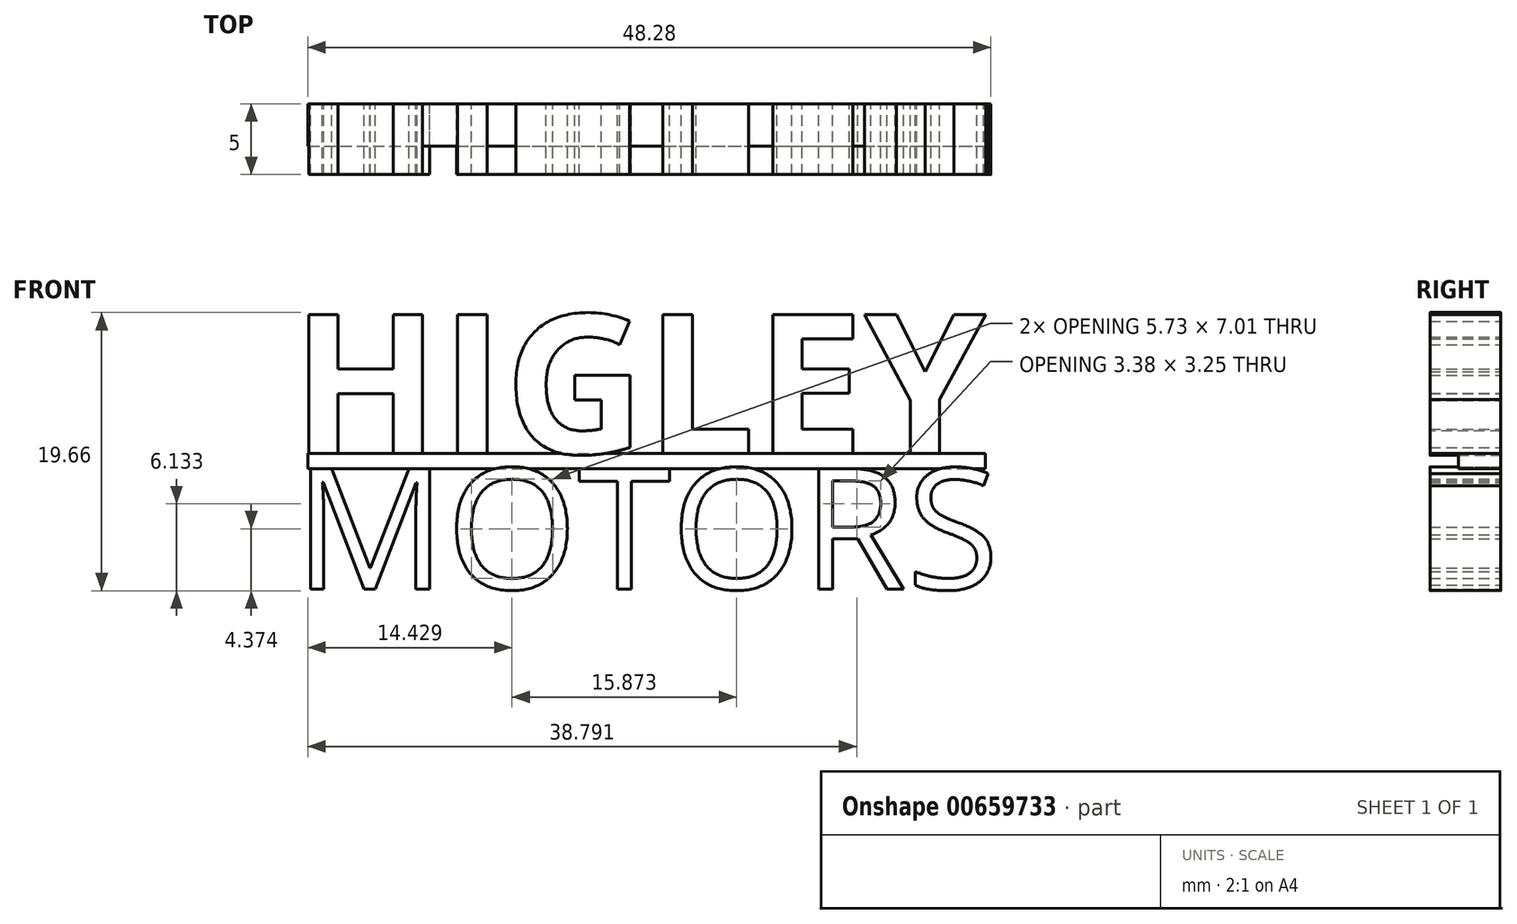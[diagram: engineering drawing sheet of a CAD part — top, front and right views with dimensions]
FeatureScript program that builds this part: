
annotation { "Feature Type Name" : "Feature", "Feature Type Description" : "" }
export const myFeature = defineFeature(function(context is Context, id is Id, definition is map)
    precondition{}
    {
        {
            var Q0;
            Q0=qCreatedBy(makeId("Front.planeOp"),FACE);
            var sketch = newSketch(context, id + "F0", { "sketchPlane" : qUnion([Q0])});
            skText(sketch, "E0", { "text": "HIGLEY", "fontName": "OpenSans-Bold.ttf"});
            const initialGuessF0  = {"E0": [-0.0133, 0, 1, 0, 0.0099]};
            skSetInitialGuess(sketch, initialGuessF0);
            skSolve(sketch);
        }
        {
            var Q0;
            Q0 = qSketchRegion(id + "F0", true);
            extrude(context, id + "F1", {"entities" : qUnion([Q0]), "depth" : 5 * mm, "offsetDistance" : 25 * mm});
        }
        {
            var Q0;
            Q0=qCreatedBy(makeId("Front.planeOp"),FACE);
            var sketch = newSketch(context, id + "F2", { "sketchPlane" : qUnion([Q0])});
            skText(sketch, "E1", { "text": "MOTORS", "fontName": "OpenSans-Regular.ttf"});
            const initialGuessF2  = {"E1": [-0.0116, -0.00858, 1, 0, 0.00858]};
            skSetInitialGuess(sketch, initialGuessF2);
            skSolve(sketch);
        }
        {
            var Q0;
            Q0 = qSketchRegion(id + "F2", true);
            extrude(context, id + "F3", {"entities" : qUnion([Q0]), "depth" : 5 * mm, "offsetDistance" : 25 * mm});
        }
        {
            var Q0;
            Q0=makeQuery(id+"F3.opExtrude","SWEPT_BODY",BODY,{"disambiguationData":[OSD([sQuery(id+"F2.wireOp",EDGE,"E1.sketch_text.stroke-0"),sQuery(id+"F2.wireOp",EDGE,"E1.sketch_text.stroke-1"),sQuery(id+"F2.wireOp",EDGE,"E1.sketch_text.stroke-2"),sQuery(id+"F2.wireOp",EDGE,"E1.sketch_text.stroke-3"),sQuery(id+"F2.wireOp",EDGE,"E1.sketch_text.stroke-4"),sQuery(id+"F2.wireOp",EDGE,"E1.sketch_text.stroke-5"),sQuery(id+"F2.wireOp",EDGE,"E1.sketch_text.stroke-6"),sQuery(id+"F2.wireOp",EDGE,"E1.sketch_text.stroke-7"),sQuery(id+"F2.wireOp",EDGE,"E1.sketch_text.stroke-8"),sQuery(id+"F2.wireOp",EDGE,"E1.sketch_text.stroke-9"),sQuery(id+"F2.wireOp",EDGE,"E1.sketch_text.stroke-10"),sQuery(id+"F2.wireOp",EDGE,"E1.sketch_text.stroke-11"),sQuery(id+"F2.wireOp",EDGE,"E1.sketch_text.stroke-12"),sQuery(id+"F2.wireOp",EDGE,"E1.sketch_text.stroke-13"),sQuery(id+"F2.wireOp",EDGE,"E1.sketch_text.stroke-14"),sQuery(id+"F2.wireOp",EDGE,"E1.sketch_text.stroke-15"),sQuery(id+"F2.wireOp",EDGE,"E1.sketch_text.stroke-16"),sQuery(id+"F2.wireOp",EDGE,"E1.sketch_text.stroke-17")])]});
            var Q1;
            Q1=makeQuery(id+"F3.opExtrude","SWEPT_BODY",BODY,{"disambiguationData":[OSD([sQuery(id+"F2.wireOp",EDGE,"E1.sketch_text.stroke-18"),sQuery(id+"F2.wireOp",EDGE,"E1.sketch_text.stroke-19"),sQuery(id+"F2.wireOp",EDGE,"E1.sketch_text.stroke-20"),sQuery(id+"F2.wireOp",EDGE,"E1.sketch_text.stroke-21"),sQuery(id+"F2.wireOp",EDGE,"E1.sketch_text.stroke-22"),sQuery(id+"F2.wireOp",EDGE,"E1.sketch_text.stroke-23"),sQuery(id+"F2.wireOp",EDGE,"E1.sketch_text.stroke-24"),sQuery(id+"F2.wireOp",EDGE,"E1.sketch_text.stroke-25"),sQuery(id+"F2.wireOp",EDGE,"E1.sketch_text.stroke-26"),sQuery(id+"F2.wireOp",EDGE,"E1.sketch_text.stroke-27"),sQuery(id+"F2.wireOp",EDGE,"E1.sketch_text.stroke-28"),sQuery(id+"F2.wireOp",EDGE,"E1.sketch_text.stroke-29"),sQuery(id+"F2.wireOp",EDGE,"E1.sketch_text.stroke-30"),sQuery(id+"F2.wireOp",EDGE,"E1.sketch_text.stroke-31"),sQuery(id+"F2.wireOp",EDGE,"E1.sketch_text.stroke-32"),sQuery(id+"F2.wireOp",EDGE,"E1.sketch_text.stroke-33")])]});
            var Q2;
            Q2=makeQuery(id+"F3.opExtrude","SWEPT_BODY",BODY,{"disambiguationData":[OSD([sQuery(id+"F2.wireOp",EDGE,"E1.sketch_text.stroke-34"),sQuery(id+"F2.wireOp",EDGE,"E1.sketch_text.stroke-35"),sQuery(id+"F2.wireOp",EDGE,"E1.sketch_text.stroke-36"),sQuery(id+"F2.wireOp",EDGE,"E1.sketch_text.stroke-37"),sQuery(id+"F2.wireOp",EDGE,"E1.sketch_text.stroke-38"),sQuery(id+"F2.wireOp",EDGE,"E1.sketch_text.stroke-39"),sQuery(id+"F2.wireOp",EDGE,"E1.sketch_text.stroke-40"),sQuery(id+"F2.wireOp",EDGE,"E1.sketch_text.stroke-41")])]});
            var Q3;
            Q3=makeQuery(id+"F3.opExtrude","SWEPT_BODY",BODY,{"disambiguationData":[OSD([sQuery(id+"F2.wireOp",EDGE,"E1.sketch_text.stroke-42"),sQuery(id+"F2.wireOp",EDGE,"E1.sketch_text.stroke-43"),sQuery(id+"F2.wireOp",EDGE,"E1.sketch_text.stroke-44"),sQuery(id+"F2.wireOp",EDGE,"E1.sketch_text.stroke-45"),sQuery(id+"F2.wireOp",EDGE,"E1.sketch_text.stroke-46"),sQuery(id+"F2.wireOp",EDGE,"E1.sketch_text.stroke-47"),sQuery(id+"F2.wireOp",EDGE,"E1.sketch_text.stroke-48"),sQuery(id+"F2.wireOp",EDGE,"E1.sketch_text.stroke-49"),sQuery(id+"F2.wireOp",EDGE,"E1.sketch_text.stroke-50"),sQuery(id+"F2.wireOp",EDGE,"E1.sketch_text.stroke-51"),sQuery(id+"F2.wireOp",EDGE,"E1.sketch_text.stroke-52"),sQuery(id+"F2.wireOp",EDGE,"E1.sketch_text.stroke-53"),sQuery(id+"F2.wireOp",EDGE,"E1.sketch_text.stroke-54"),sQuery(id+"F2.wireOp",EDGE,"E1.sketch_text.stroke-55"),sQuery(id+"F2.wireOp",EDGE,"E1.sketch_text.stroke-56"),sQuery(id+"F2.wireOp",EDGE,"E1.sketch_text.stroke-57")])]});
            var Q4;
            Q4=makeQuery(id+"F3.opExtrude","SWEPT_BODY",BODY,{"disambiguationData":[OSD([sQuery(id+"F2.wireOp",EDGE,"E1.sketch_text.stroke-58"),sQuery(id+"F2.wireOp",EDGE,"E1.sketch_text.stroke-59"),sQuery(id+"F2.wireOp",EDGE,"E1.sketch_text.stroke-60"),sQuery(id+"F2.wireOp",EDGE,"E1.sketch_text.stroke-61"),sQuery(id+"F2.wireOp",EDGE,"E1.sketch_text.stroke-62"),sQuery(id+"F2.wireOp",EDGE,"E1.sketch_text.stroke-63"),sQuery(id+"F2.wireOp",EDGE,"E1.sketch_text.stroke-64"),sQuery(id+"F2.wireOp",EDGE,"E1.sketch_text.stroke-65"),sQuery(id+"F2.wireOp",EDGE,"E1.sketch_text.stroke-66"),sQuery(id+"F2.wireOp",EDGE,"E1.sketch_text.stroke-67"),sQuery(id+"F2.wireOp",EDGE,"E1.sketch_text.stroke-68"),sQuery(id+"F2.wireOp",EDGE,"E1.sketch_text.stroke-69"),sQuery(id+"F2.wireOp",EDGE,"E1.sketch_text.stroke-70"),sQuery(id+"F2.wireOp",EDGE,"E1.sketch_text.stroke-71"),sQuery(id+"F2.wireOp",EDGE,"E1.sketch_text.stroke-72"),sQuery(id+"F2.wireOp",EDGE,"E1.sketch_text.stroke-73"),sQuery(id+"F2.wireOp",EDGE,"E1.sketch_text.stroke-74"),sQuery(id+"F2.wireOp",EDGE,"E1.sketch_text.stroke-75")])]});
            var Q5;
            Q5=makeQuery(id+"F3.opExtrude","SWEPT_BODY",BODY,{"disambiguationData":[OSD([sQuery(id+"F2.wireOp",EDGE,"E1.sketch_text.stroke-76"),sQuery(id+"F2.wireOp",EDGE,"E1.sketch_text.stroke-77"),sQuery(id+"F2.wireOp",EDGE,"E1.sketch_text.stroke-78"),sQuery(id+"F2.wireOp",EDGE,"E1.sketch_text.stroke-79"),sQuery(id+"F2.wireOp",EDGE,"E1.sketch_text.stroke-80"),sQuery(id+"F2.wireOp",EDGE,"E1.sketch_text.stroke-81"),sQuery(id+"F2.wireOp",EDGE,"E1.sketch_text.stroke-82"),sQuery(id+"F2.wireOp",EDGE,"E1.sketch_text.stroke-83"),sQuery(id+"F2.wireOp",EDGE,"E1.sketch_text.stroke-84"),sQuery(id+"F2.wireOp",EDGE,"E1.sketch_text.stroke-85"),sQuery(id+"F2.wireOp",EDGE,"E1.sketch_text.stroke-86"),sQuery(id+"F2.wireOp",EDGE,"E1.sketch_text.stroke-87"),sQuery(id+"F2.wireOp",EDGE,"E1.sketch_text.stroke-88"),sQuery(id+"F2.wireOp",EDGE,"E1.sketch_text.stroke-89"),sQuery(id+"F2.wireOp",EDGE,"E1.sketch_text.stroke-90"),sQuery(id+"F2.wireOp",EDGE,"E1.sketch_text.stroke-91"),sQuery(id+"F2.wireOp",EDGE,"E1.sketch_text.stroke-92"),sQuery(id+"F2.wireOp",EDGE,"E1.sketch_text.stroke-93"),sQuery(id+"F2.wireOp",EDGE,"E1.sketch_text.stroke-94"),sQuery(id+"F2.wireOp",EDGE,"E1.sketch_text.stroke-95"),sQuery(id+"F2.wireOp",EDGE,"E1.sketch_text.stroke-96"),sQuery(id+"F2.wireOp",EDGE,"E1.sketch_text.stroke-97"),sQuery(id+"F2.wireOp",EDGE,"E1.sketch_text.stroke-98"),sQuery(id+"F2.wireOp",EDGE,"E1.sketch_text.stroke-99"),sQuery(id+"F2.wireOp",EDGE,"E1.sketch_text.stroke-100")])]});
            transform(context, id + "F4", {"entities" : qUnion([Q0, Q1, Q2, Q3, Q4, Q5]), "transformType" : TransformType.TRANSLATION_3D, "dx" : -1.5 * mm, "dy" : 0 * mm, "dz" : -1 * mm, "makeCopy" : false});
        }
        {
            var Q0;
            Q0=qCreatedBy(makeId("Front.planeOp"),FACE);
            var sketch = newSketch(context, id + "F5", { "sketchPlane" : qUnion([Q0])});
            skLineSegment(sketch, "E2.bottom", {"start": v(-12.13, 0) * mm, "end": v(35.74, 0) * mm});
            skLineSegment(sketch, "E2.top", {"start": v(-12.13, -1.07) * mm, "end": v(35.74, -1.07) * mm});
            skLineSegment(sketch, "E2.left", {"start": v(-12.13, 0) * mm, "end": v(-12.13, -1.07) * mm});
            skLineSegment(sketch, "E2.right", {"start": v(35.74, 0) * mm, "end": v(35.74, -1.07) * mm});
            skSolve(sketch);
        }
        {
            var Q0;
            Q0 = qSketchRegion(id + "F5", true);
            extrude(context, id + "F6", {"entities" : qUnion([Q0]), "depth" : 3 * mm, "offsetDistance" : 25 * mm});
        }
    });
